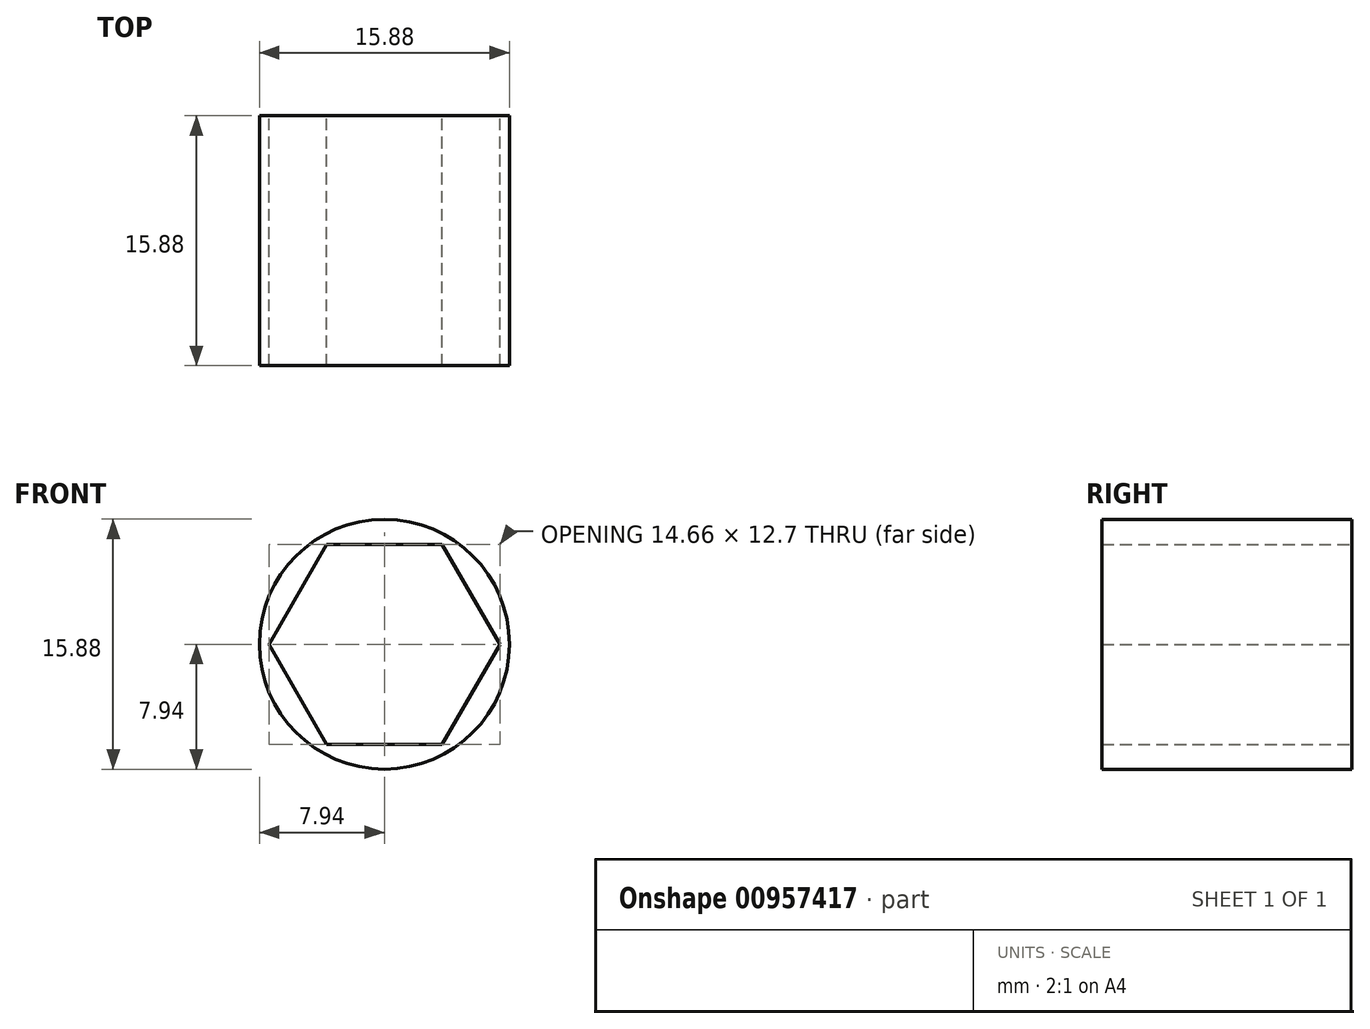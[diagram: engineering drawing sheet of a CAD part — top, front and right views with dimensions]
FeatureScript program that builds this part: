
annotation { "Feature Type Name" : "Feature", "Feature Type Description" : "" }
export const myFeature = defineFeature(function(context is Context, id is Id, definition is map)
    precondition{}
    {
        {
            var Q0;
            Q0=qCreatedBy(makeId("Front.planeOp"),FACE);
            var sketch = newSketch(context, id + "F0", { "sketchPlane" : qUnion([Q0])});
            skCircle(sketch, "E0", {"center": v(0, 0) * mm, "radius": 7.94 * mm});
            skCircle(sketch, "E1.cCircle", {"center": v(0, 0) * mm, "radius": 6.35 * mm, "construction": true});
            skLineSegment(sketch, "E1.0", {"start": v(-3.67, 6.35) * mm, "end": v(3.67, 6.35) * mm});
            skLineSegment(sketch, "E1.1", {"start": v(3.67, 6.35) * mm, "end": v(7.33, 0) * mm});
            skLineSegment(sketch, "E1.2", {"start": v(7.33, 0) * mm, "end": v(3.67, -6.35) * mm});
            skLineSegment(sketch, "E1.3", {"start": v(3.67, -6.35) * mm, "end": v(-3.67, -6.35) * mm});
            skLineSegment(sketch, "E1.4", {"start": v(-3.67, -6.35) * mm, "end": v(-7.33, 0) * mm});
            skLineSegment(sketch, "E1.5", {"start": v(-7.33, 0) * mm, "end": v(-3.67, 6.35) * mm});
            skPoint(sketch, "E1.0.midPoint", {"position": v(0, 6.35) * mm});
            skSolve(sketch);
        }
        {
            var Q0;
            Q0 = qSketchRegion(id + "F0", true);
            extrude(context, id + "F1", {"entities" : qUnion([Q0]), "depth" : 15.88 * mm, "offsetDistance" : 25.4 * mm});
        }
    });
